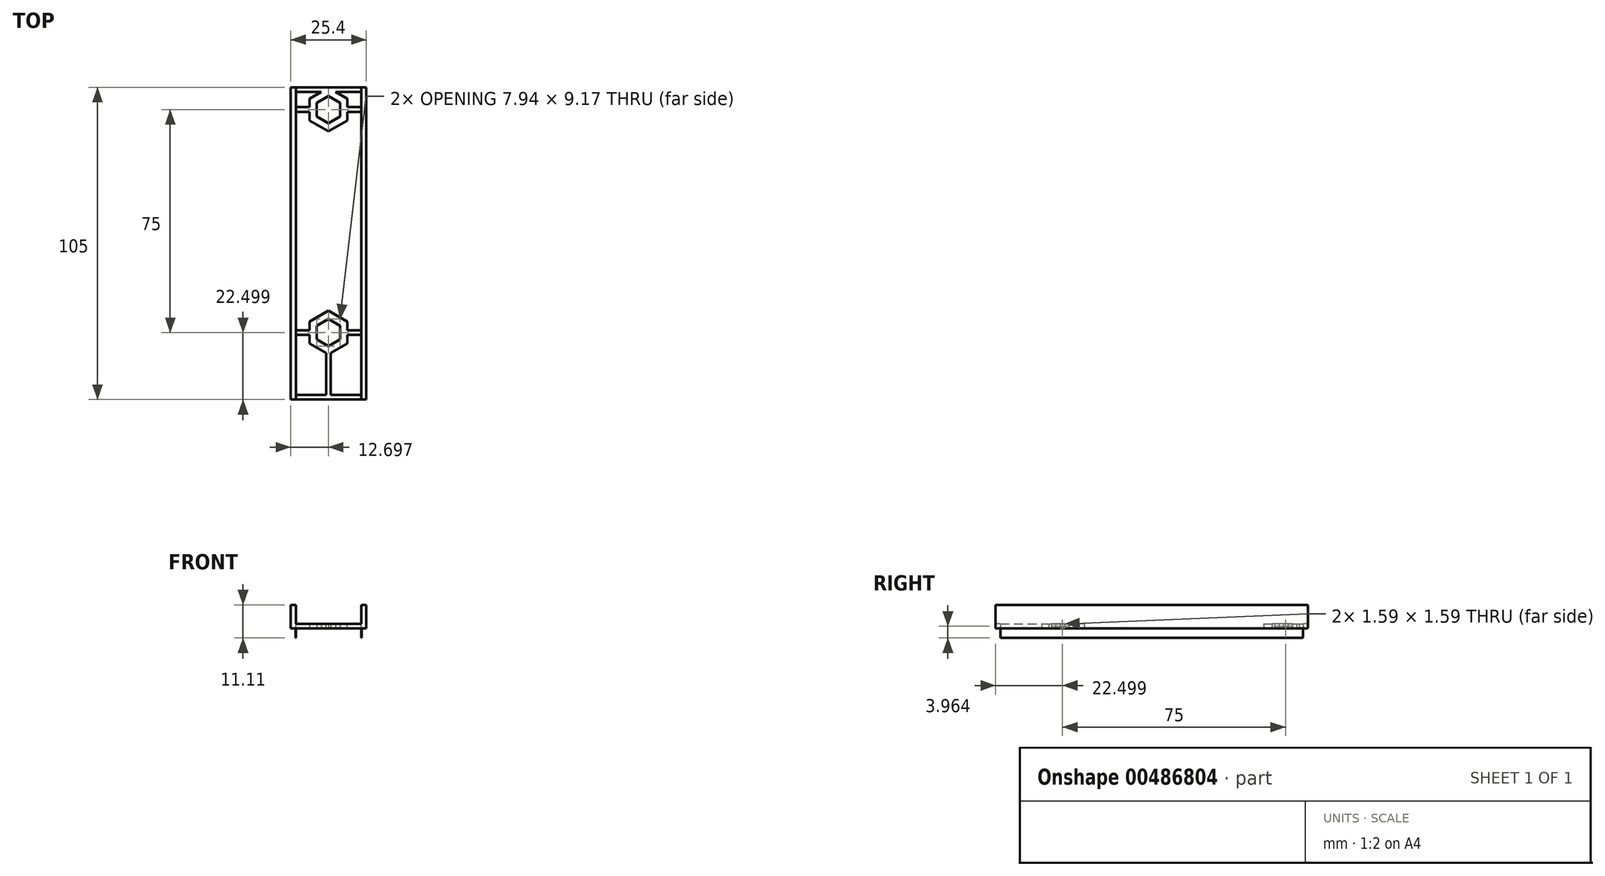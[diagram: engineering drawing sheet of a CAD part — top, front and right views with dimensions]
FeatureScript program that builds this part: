
annotation { "Feature Type Name" : "Feature", "Feature Type Description" : "" }
export const myFeature = defineFeature(function(context is Context, id is Id, definition is map)
    precondition{}
    {
        {
            var Q0;
            Q0=qCreatedBy(makeId("Top.planeOp"),FACE);
            var sketch = newSketch(context, id + "F0", { "sketchPlane" : qUnion([Q0])});
            skLineSegment(sketch, "E0.bottom", {"start": v(-43, -50.26) * mm, "end": v(-68.4, -50.26) * mm});
            skLineSegment(sketch, "E0.top", {"start": v(-43, 54.74) * mm, "end": v(-68.4, 54.74) * mm});
            skLineSegment(sketch, "E0.left", {"start": v(-43, -50.26) * mm, "end": v(-43, 54.74) * mm});
            skLineSegment(sketch, "E0.right", {"start": v(-68.4, -50.26) * mm, "end": v(-68.4, 54.74) * mm});
            skSolve(sketch);
        }
        {
            var Q0;
            Q0 = qSketchRegion(id + "F0", true);
            extrude(context, id + "F1", {"entities" : qUnion([Q0]), "depth" : 12.7 * mm});
        }
        {
            var Q0;
            Q0=makeQuery(id+"F1.opExtrude","CAP_FACE",FACE,{"disambiguationData":[OSD([sQuery(id+"F0.wireOp",EDGE,"E0.bottom"),sQuery(id+"F0.wireOp",EDGE,"E0.top"),sQuery(id+"F0.wireOp",EDGE,"E0.left"),sQuery(id+"F0.wireOp",EDGE,"E0.right")])],"isStart":false});
            var sketch = newSketch(context, id + "F2", { "sketchPlane" : qUnion([Q0])});
            skCircle(sketch, "E1", {"center": v(-55.7, -27.76) * mm, "radius": 1.59 * mm});
            skPoint(sketch, "E1.centerSnap0", {"position": v(-55.7, -50.26) * mm});
            skSolve(sketch);
        }
        {
            var Q0;
            Q0 = qSketchRegion(id + "F2", true);
            extrude(context, id + "F3", {"entities" : qUnion([Q0]), "operationType" : NewBodyOperationType.REMOVE, "oppositeDirection" : true, "depth" : 25.4 * mm});
        }
        {
            var Q0;
            Q0=makeQuery(id+"F1.opExtrude","SWEPT_FACE",FACE,{"disambiguationData":[OSD([sQuery(id+"F0.wireOp",EDGE,"E0.bottom")])]});
            var sketch = newSketch(context, id + "F4", { "sketchPlane" : qUnion([Q0])});
            skCircle(sketch, "E2", {"center": v(-55.7, 19.05) * mm, "radius": 12.7 * mm});
            skSolve(sketch);
        }
        {
            var Q0;
            Q0=makeQuery(id+"F1.opExtrude","CAP_FACE",FACE,{"disambiguationData":[OSD([sQuery(id+"F0.wireOp",EDGE,"E0.bottom"),sQuery(id+"F0.wireOp",EDGE,"E0.top"),sQuery(id+"F0.wireOp",EDGE,"E0.left"),sQuery(id+"F0.wireOp",EDGE,"E0.right")])],"isStart":false});
            var sketch = newSketch(context, id + "F5", { "sketchPlane" : qUnion([Q0])});
            skCircle(sketch, "E3", {"center": v(-55.7, 47.24) * mm, "radius": 1.59 * mm});
            skPoint(sketch, "E3.centerSnap0", {"position": v(-55.7, 54.74) * mm});
            skSolve(sketch);
        }
        {
            var Q0;
            Q0 = qSketchRegion(id + "F5", true);
            extrude(context, id + "F6", {"entities" : qUnion([Q0]), "operationType" : NewBodyOperationType.REMOVE, "oppositeDirection" : true, "depth" : 25.4 * mm});
        }
        {
            var Q0;
            Q0 = qSketchRegion(id + "F4", true);
            extrude(context, id + "F7", {"entities" : qUnion([Q0]), "operationType" : NewBodyOperationType.REMOVE, "endBound" : BoundingType.THROUGH_ALL, "oppositeDirection" : true, "depth" : 25.4 * mm});
        }
        {
            var Q0;
            Q0=makeQuery(id+"F1.opExtrude","SWEPT_FACE",FACE,{"disambiguationData":[OSD([sQuery(id+"F0.wireOp",EDGE,"E0.bottom")])]});
            var sketch = newSketch(context, id + "F8", { "sketchPlane" : qUnion([Q0])});
            skLineSegment(sketch, "E4.bottom", {"start": v(-68.4, 0) * mm, "end": v(-43, 0) * mm});
            skLineSegment(sketch, "E4.top", {"start": v(-68.4, 4.76) * mm, "end": v(-43, 4.76) * mm});
            skLineSegment(sketch, "E4.left", {"start": v(-68.4, 0) * mm, "end": v(-68.4, 4.76) * mm});
            skLineSegment(sketch, "E4.right", {"start": v(-43, 0) * mm, "end": v(-43, 4.76) * mm});
            skSolve(sketch);
        }
        {
            var Q0;
            Q0 = qSketchRegion(id + "F8", true);
            extrude(context, id + "F9", {"entities" : qUnion([Q0]), "operationType" : NewBodyOperationType.REMOVE, "endBound" : BoundingType.THROUGH_ALL, "oppositeDirection" : true, "depth" : 25.4 * mm});
        }
        {
            var Q0;
            Q0=makeQuery(id+"F9.boolean.opBoolean","COPY",FACE,{"derivedFrom":makeQuery(id+"F9.opExtrude","SWEPT_FACE",FACE,{"disambiguationData":[OSD([sQuery(id+"F8.wireOp",EDGE,"E4.top")])]})});
            var sketch = newSketch(context, id + "F10", { "sketchPlane" : qUnion([Q0])});
            skCircle(sketch, "E5.cCircle", {"center": v(-55.7, 27.76) * mm, "radius": 3.97 * mm, "construction": true});
            skLineSegment(sketch, "E5.0", {"start": v(-51.72, 30.05) * mm, "end": v(-51.72, 25.47) * mm});
            skLineSegment(sketch, "E5.1", {"start": v(-51.72, 25.47) * mm, "end": v(-55.7, 23.18) * mm});
            skLineSegment(sketch, "E5.2", {"start": v(-55.7, 23.18) * mm, "end": v(-59.66, 25.47) * mm});
            skLineSegment(sketch, "E5.3", {"start": v(-59.66, 25.47) * mm, "end": v(-59.66, 30.05) * mm});
            skLineSegment(sketch, "E5.4", {"start": v(-59.66, 30.05) * mm, "end": v(-55.7, 32.34) * mm});
            skLineSegment(sketch, "E5.5", {"start": v(-55.7, 32.34) * mm, "end": v(-51.72, 30.05) * mm});
            skPoint(sketch, "E5.0.midPoint", {"position": v(-51.72, 27.76) * mm});
            skCircle(sketch, "E6.cCircle", {"center": v(-55.7, -47.24) * mm, "radius": 3.97 * mm, "construction": true});
            skLineSegment(sketch, "E6.0", {"start": v(-51.72, -44.95) * mm, "end": v(-51.72, -49.53) * mm});
            skLineSegment(sketch, "E6.1", {"start": v(-51.72, -49.53) * mm, "end": v(-55.7, -51.82) * mm});
            skLineSegment(sketch, "E6.2", {"start": v(-55.7, -51.82) * mm, "end": v(-59.66, -49.53) * mm});
            skLineSegment(sketch, "E6.3", {"start": v(-59.66, -49.53) * mm, "end": v(-59.66, -44.95) * mm});
            skLineSegment(sketch, "E6.4", {"start": v(-59.66, -44.95) * mm, "end": v(-55.7, -42.66) * mm});
            skLineSegment(sketch, "E6.5", {"start": v(-55.7, -42.66) * mm, "end": v(-51.72, -44.95) * mm});
            skPoint(sketch, "E6.0.midPoint", {"position": v(-51.72, -47.24) * mm});
            skSolve(sketch);
        }
        {
            var Q0;
            Q0 = qSketchRegion(id + "F10", true);
            extrude(context, id + "F11", {"entities" : qUnion([Q0]), "operationType" : NewBodyOperationType.REMOVE, "oppositeDirection" : true, "depth" : 25.4 * mm});
        }
        {
            var Q0;
            Q0=makeQuery(id+"F9.boolean.opBoolean","COPY",FACE,{"derivedFrom":makeQuery(id+"F9.opExtrude","SWEPT_FACE",FACE,{"disambiguationData":[OSD([sQuery(id+"F8.wireOp",EDGE,"E4.top")])]})});
            extrude(context, id + "F12", {"entities" : qUnion([Q0]), "operationType" : NewBodyOperationType.ADD, "depth" : 1 / 203.2 * mm});
        }
        {
            var Q0;
            Q0=makeQuery(id+"F12.opExtrude","CAP_FACE",FACE,{"disambiguationData":[OSD([sQuery(id+"F8.wireOp",EDGE,"E4.top")])],"isStart":false});
            var sketch = newSketch(context, id + "F13", { "sketchPlane" : qUnion([Q0])});
            skCircle(sketch, "E7.cCircle", {"center": v(-55.7, -47.24) * mm, "radius": 6.35 * mm, "construction": true});
            skPoint(sketch, "E7.cCircle.centerSnap0", {"position": v(-51.72, -47.24) * mm});
            skLineSegment(sketch, "E7.0", {"start": v(-62.04, -43.57) * mm, "end": v(-55.7, -39.9) * mm});
            skLineSegment(sketch, "E7.1", {"start": v(-55.7, -39.9) * mm, "end": v(-49.34, -43.57) * mm});
            skLineSegment(sketch, "E7.2", {"start": v(-49.34, -43.57) * mm, "end": v(-49.34, -50.9) * mm});
            skLineSegment(sketch, "E7.3", {"start": v(-49.34, -50.9) * mm, "end": v(-55.7, -54.57) * mm});
            skLineSegment(sketch, "E7.4", {"start": v(-55.7, -54.57) * mm, "end": v(-62.04, -50.9) * mm});
            skLineSegment(sketch, "E7.5", {"start": v(-62.04, -50.9) * mm, "end": v(-62.04, -43.57) * mm});
            skPoint(sketch, "E7.0.midPoint", {"position": v(-58.87, -41.74) * mm});
            skCircle(sketch, "E8.cCircle", {"center": v(-55.7, 27.76) * mm, "radius": 6.35 * mm, "construction": true});
            skPoint(sketch, "E8.cCircle.centerSnap0", {"position": v(-51.72, 27.76) * mm});
            skLineSegment(sketch, "E8.0", {"start": v(-62.04, 24.1) * mm, "end": v(-62.04, 31.43) * mm});
            skLineSegment(sketch, "E8.1", {"start": v(-62.04, 31.43) * mm, "end": v(-55.7, 35.1) * mm});
            skLineSegment(sketch, "E8.2", {"start": v(-55.7, 35.1) * mm, "end": v(-49.34, 31.43) * mm});
            skLineSegment(sketch, "E8.3", {"start": v(-49.34, 31.43) * mm, "end": v(-49.34, 24.1) * mm});
            skLineSegment(sketch, "E8.4", {"start": v(-49.34, 24.1) * mm, "end": v(-55.7, 20.43) * mm});
            skLineSegment(sketch, "E8.5", {"start": v(-55.7, 20.43) * mm, "end": v(-62.04, 24.1) * mm});
            skPoint(sketch, "E8.0.midPoint", {"position": v(-62.04, 27.76) * mm});
            skLineSegment(sketch, "E9", {"start": v(-53.23, -53.15) * mm, "end": v(-44.58, -53.15) * mm});
            skLineSegment(sketch, "E10", {"start": v(-44.58, -53.15) * mm, "end": v(-44.58, 48.67) * mm});
            skLineSegment(sketch, "E11", {"start": v(-44.58, 48.67) * mm, "end": v(-66.8, 48.67) * mm});
            skLineSegment(sketch, "E12", {"start": v(-66.8, 48.67) * mm, "end": v(-66.8, -53.15) * mm});
            skLineSegment(sketch, "E13", {"start": v(-66.8, -53.15) * mm, "end": v(-58.15, -53.15) * mm});
            skSolve(sketch);
        }
        {
            var Q0;
            Q0=makeQuery(id+"F13.imprint","IMPRINT",FACE,{"disambiguationData":[TD([[makeQuery(id+"F13.imprint","IMPRINT",EDGE,{"derivedFrom":sQuery(id+"F13.wireOp",EDGE,"E7.0")}),1.0]])]});
            extrude(context, id + "F14", {"entities" : qUnion([Q0]), "operationType" : NewBodyOperationType.REMOVE, "endBound" : BoundingType.THROUGH_ALL, "oppositeDirection" : true, "depth" : 25.4 * mm});
        }
        {
            var Q0;
            {var subQ3=sQuery(id+"F8.wireOp",EDGE,"E4.top");var subQ9=sQuery(id+"F0.wireOp",EDGE,"E0.bottom");Q0=makeQuery(id+"F14.boolean.opBoolean","SPLIT",FACE,{"disambiguationData":[TD([makeQuery(id+"F1.opExtrude","SWEPT_FACE",FACE,{"disambiguationData":[OSD([subQ9])]})])],"derivedFrom":makeQuery(id+"F12.opExtrude","CAP_FACE",FACE,{"disambiguationData":[OSD([subQ3])],"isStart":false})});}
            var sketch = newSketch(context, id + "F15", { "sketchPlane" : qUnion([Q0])});
            skLineSegment(sketch, "E14.bottom", {"start": v(-49.34, -48.03) * mm, "end": v(-43, -48.03) * mm});
            skLineSegment(sketch, "E14.top", {"start": v(-49.34, -46.44) * mm, "end": v(-43, -46.44) * mm});
            skLineSegment(sketch, "E14.left", {"start": v(-49.34, -48.03) * mm, "end": v(-49.34, -46.44) * mm});
            skLineSegment(sketch, "E14.right", {"start": v(-43, -48.03) * mm, "end": v(-43, -46.44) * mm});
            skLineSegment(sketch, "E15.bottom", {"start": v(-62.04, -48.03) * mm, "end": v(-68.4, -48.03) * mm});
            skLineSegment(sketch, "E15.top", {"start": v(-62.04, -46.44) * mm, "end": v(-68.4, -46.44) * mm});
            skLineSegment(sketch, "E15.left", {"start": v(-62.04, -48.03) * mm, "end": v(-62.04, -46.44) * mm});
            skLineSegment(sketch, "E15.right", {"start": v(-68.4, -48.03) * mm, "end": v(-68.4, -46.44) * mm});
            skSolve(sketch);
        }
        {
            var Q0;
            {var subQ0=sQuery(id+"F15.wireOp",EDGE,"E14.left");Q0=makeQuery(id+"F15.imprint","IMPRINT",FACE,{"disambiguationData":[TD([[makeQuery(id+"F15.imprint","IMPRINT",EDGE,{"derivedFrom":subQ0}),1.0]])]});}
            var Q1;
            {var subQ0=sQuery(id+"F15.wireOp",EDGE,"E15.left");Q1=makeQuery(id+"F15.imprint","IMPRINT",FACE,{"disambiguationData":[TD([[makeQuery(id+"F15.imprint","IMPRINT",EDGE,{"derivedFrom":subQ0}),1.0]])]});}
            extrude(context, id + "F16", {"entities" : qUnion([Q0, Q1]), "operationType" : NewBodyOperationType.ADD, "oppositeDirection" : true, "depth" : 6.35 * mm});
        }
        {
            var Q0;
            {var subQ0=sQuery(id+"F13.wireOp",EDGE,"E12");var subQ1=sQuery(id+"F13.wireOp",EDGE,"E10");var subQ5=sQuery(id+"F8.wireOp",EDGE,"E4.top");var subQ11=sQuery(id+"F0.wireOp",EDGE,"E0.bottom");Q0=makeQuery(id+"F16.boolean.opBoolean","MERGE",FACE,{"derivedFrom":[makeQuery(id+"F14.boolean.opBoolean","SPLIT",FACE,{"disambiguationData":[TD([makeQuery(id+"F1.opExtrude","SWEPT_FACE",FACE,{"disambiguationData":[OSD([subQ11])]})])],"derivedFrom":makeQuery(id+"F12.opExtrude","CAP_FACE",FACE,{"disambiguationData":[OSD([subQ5])],"isStart":false})}),makeQuery(id+"F16.opExtrude","CAP_FACE",FACE,{"disambiguationData":[OSD([subQ1,sQuery(id+"F15.wireOp",EDGE,"E14.bottom"),sQuery(id+"F15.wireOp",EDGE,"E14.top"),sQuery(id+"F15.wireOp",EDGE,"E14.left")])],"isStart":true}),makeQuery(id+"F16.opExtrude","CAP_FACE",FACE,{"disambiguationData":[OSD([subQ0,sQuery(id+"F15.wireOp",EDGE,"E15.bottom"),sQuery(id+"F15.wireOp",EDGE,"E15.top"),sQuery(id+"F15.wireOp",EDGE,"E15.left")])],"isStart":true})]});}
            var sketch = newSketch(context, id + "F17", { "sketchPlane" : qUnion([Q0])});
            skLineSegment(sketch, "E16.bottom", {"start": v(-61.05, 28.56) * mm, "end": v(-66.8, 28.56) * mm});
            skLineSegment(sketch, "E16.top", {"start": v(-61.05, 26.97) * mm, "end": v(-66.8, 26.97) * mm});
            skLineSegment(sketch, "E16.left", {"start": v(-61.05, 28.56) * mm, "end": v(-61.05, 26.97) * mm});
            skLineSegment(sketch, "E16.right", {"start": v(-66.8, 28.56) * mm, "end": v(-66.8, 26.97) * mm});
            skPoint(sketch, "E17.firstSnap0", {"position": v(-63.93, 26.97) * mm});
            skLineSegment(sketch, "E17.bottom", {"start": v(-50.1, 26.97) * mm, "end": v(-44.58, 26.97) * mm});
            skLineSegment(sketch, "E17.top", {"start": v(-50.1, 28.56) * mm, "end": v(-44.58, 28.56) * mm});
            skLineSegment(sketch, "E17.left", {"start": v(-50.1, 26.97) * mm, "end": v(-50.1, 28.56) * mm});
            skLineSegment(sketch, "E17.right", {"start": v(-44.58, 26.97) * mm, "end": v(-44.58, 28.56) * mm});
            skLineSegment(sketch, "E18.bottom", {"start": v(-56.49, 33.74) * mm, "end": v(-54.9, 33.74) * mm});
            skLineSegment(sketch, "E18.top", {"start": v(-56.49, 48.67) * mm, "end": v(-54.9, 48.67) * mm});
            skLineSegment(sketch, "E18.left", {"start": v(-56.49, 33.74) * mm, "end": v(-56.49, 48.67) * mm});
            skLineSegment(sketch, "E18.right", {"start": v(-54.9, 33.74) * mm, "end": v(-54.9, 48.67) * mm});
            skSolve(sketch);
        }
        {
            var Q0;
            Q0 = qSketchRegion(id + "F17", true);
            extrude(context, id + "F18", {"entities" : qUnion([Q0]), "oppositeDirection" : true, "depth" : 4.23 * mm});
        }
        {
            var Q0;
            Q0=makeQuery(id+"F18.opExtrude","SWEPT_BODY",BODY,{"disambiguationData":[OSD([sQuery(id+"F17.wireOp",EDGE,"E17.bottom"),sQuery(id+"F17.wireOp",EDGE,"E17.top"),sQuery(id+"F17.wireOp",EDGE,"E17.left"),sQuery(id+"F17.wireOp",EDGE,"E17.right")])]});
            var Q1;
            Q1=makeQuery(id+"F18.opExtrude","SWEPT_BODY",BODY,{"disambiguationData":[OSD([sQuery(id+"F17.wireOp",EDGE,"E18.bottom"),sQuery(id+"F17.wireOp",EDGE,"E18.top"),sQuery(id+"F17.wireOp",EDGE,"E18.left"),sQuery(id+"F17.wireOp",EDGE,"E18.right")])]});
            var Q2;
            Q2=makeQuery(id+"F14.boolean.opBoolean","SPLIT",BODY,{"disambiguationData":[OD(0.0)],"derivedFrom":makeQuery(id+"F1.opExtrude","SWEPT_BODY",BODY,{"disambiguationData":[OSD([sQuery(id+"F0.wireOp",EDGE,"E0.bottom"),sQuery(id+"F0.wireOp",EDGE,"E0.top"),sQuery(id+"F0.wireOp",EDGE,"E0.left"),sQuery(id+"F0.wireOp",EDGE,"E0.right")])]})});
            var Q3;
            Q3=makeQuery(id+"F14.boolean.opBoolean","SPLIT",BODY,{"disambiguationData":[OD(1.0)],"derivedFrom":makeQuery(id+"F1.opExtrude","SWEPT_BODY",BODY,{"disambiguationData":[OSD([sQuery(id+"F0.wireOp",EDGE,"E0.bottom"),sQuery(id+"F0.wireOp",EDGE,"E0.top"),sQuery(id+"F0.wireOp",EDGE,"E0.left"),sQuery(id+"F0.wireOp",EDGE,"E0.right")])]})});
            var Q4;
            Q4=makeQuery(id+"F18.opExtrude","SWEPT_BODY",BODY,{"disambiguationData":[OSD([sQuery(id+"F17.wireOp",EDGE,"E16.bottom"),sQuery(id+"F17.wireOp",EDGE,"E16.top"),sQuery(id+"F17.wireOp",EDGE,"E16.left"),sQuery(id+"F17.wireOp",EDGE,"E16.right")])]});
            booleanBodies(context, id + "F19", {"operationType" : BooleanOperationType.UNION, "tools" : qUnion([Q0, Q1, Q2, Q3, Q4])});
        }
        {
            var Q0;
            {var subQ0=sQuery(id+"F0.wireOp",EDGE,"E0.bottom");var subQ1=sQuery(id+"F0.wireOp",EDGE,"E0.top");var subQ2=sQuery(id+"F0.wireOp",EDGE,"E0.left");Q0=makeQuery(id+"F7.boolean.opBoolean","SPLIT",FACE,{"disambiguationData":[TD([makeQuery(id+"F1.opExtrude","SWEPT_FACE",FACE,{"disambiguationData":[OSD([subQ2])]})])],"derivedFrom":makeQuery(id+"F1.opExtrude","CAP_FACE",FACE,{"disambiguationData":[OSD([subQ0,subQ1,subQ2,sQuery(id+"F0.wireOp",EDGE,"E0.right")])],"isStart":false})});}
            var sketch = newSketch(context, id + "F20", { "sketchPlane" : qUnion([Q0])});
            skLineSegment(sketch, "E19.bottom", {"start": v(-44.7, -50.26) * mm, "end": v(-44.58, -50.26) * mm});
            skLineSegment(sketch, "E19.top", {"start": v(-44.7, 53.15) * mm, "end": v(-44.58, 53.15) * mm});
            skLineSegment(sketch, "E19.left", {"start": v(-44.7, -50.26) * mm, "end": v(-44.7, 53.15) * mm});
            skLineSegment(sketch, "E19.right", {"start": v(-44.58, -50.26) * mm, "end": v(-44.58, 53.15) * mm});
            skSolve(sketch);
        }
        {
            var Q0;
            {var subQ0=sQuery(id+"F0.wireOp",EDGE,"E0.bottom");var subQ1=sQuery(id+"F0.wireOp",EDGE,"E0.right");var subQ2=sQuery(id+"F0.wireOp",EDGE,"E0.top");Q0=makeQuery(id+"F7.boolean.opBoolean","SPLIT",FACE,{"disambiguationData":[TD([makeQuery(id+"F1.opExtrude","SWEPT_FACE",FACE,{"disambiguationData":[OSD([subQ1])]})])],"derivedFrom":makeQuery(id+"F1.opExtrude","CAP_FACE",FACE,{"disambiguationData":[OSD([subQ0,subQ2,sQuery(id+"F0.wireOp",EDGE,"E0.left"),subQ1])],"isStart":false})});}
            var sketch = newSketch(context, id + "F21", { "sketchPlane" : qUnion([Q0])});
            skLineSegment(sketch, "E20.bottom", {"start": v(-66.7, 53.15) * mm, "end": v(-66.8, 53.15) * mm});
            skLineSegment(sketch, "E20.top", {"start": v(-66.7, -48.67) * mm, "end": v(-66.8, -48.67) * mm});
            skLineSegment(sketch, "E20.left", {"start": v(-66.7, 53.15) * mm, "end": v(-66.7, -48.67) * mm});
            skLineSegment(sketch, "E20.right", {"start": v(-66.8, 53.15) * mm, "end": v(-66.8, -48.67) * mm});
            skSolve(sketch);
        }
        {
            var Q0;
            {var subQ0=sQuery(id+"F20.wireOp",EDGE,"E19.top");Q0=makeQuery(id+"F20.imprint","IMPRINT",FACE,{"disambiguationData":[TD([[makeQuery(id+"F20.imprint","IMPRINT",EDGE,{"derivedFrom":subQ0}),1.0]])]});}
            var Q1;
            Q1=makeQuery(id+"F21.imprint","IMPRINT",FACE,{"disambiguationData":[TD([[makeQuery(id+"F21.imprint","IMPRINT",EDGE,{"derivedFrom":sQuery(id+"F21.wireOp",EDGE,"E20.bottom")}),1.0]])]});
            extrude(context, id + "F22", {"entities" : qUnion([Q0, Q1]), "operationType" : NewBodyOperationType.ADD, "oppositeDirection" : true, "depth" : 12.7 * mm});
        }
        {
            var Q0;
            {var subQ0=sQuery(id+"F0.wireOp",EDGE,"E0.top");Q0=makeQuery(id+"F12.boolean.opBoolean","MERGE",FACE,{"derivedFrom":[makeQuery(id+"F1.opExtrude","SWEPT_FACE",FACE,{"disambiguationData":[OSD([subQ0])]}),makeQuery(id+"F12.opExtrude","SWEPT_FACE",FACE,{"disambiguationData":[OSD([subQ0,sQuery(id+"F8.wireOp",EDGE,"E4.top")])]})]});}
            var sketch = newSketch(context, id + "F23", { "sketchPlane" : qUnion([Q0])});
            skLineSegment(sketch, "E21.bottom", {"start": v(68.4, 1.59) * mm, "end": v(43, 1.59) * mm});
            skLineSegment(sketch, "E21.top", {"start": v(68.4, -4.13) * mm, "end": v(43, -4.13) * mm});
            skLineSegment(sketch, "E21.left", {"start": v(68.4, 1.59) * mm, "end": v(68.4, -4.13) * mm});
            skLineSegment(sketch, "E21.right", {"start": v(43, 1.59) * mm, "end": v(43, -4.13) * mm});
            skSolve(sketch);
        }
        {
            var Q0;
            Q0 = qSketchRegion(id + "F23", true);
            extrude(context, id + "F24", {"entities" : qUnion([Q0]), "operationType" : NewBodyOperationType.REMOVE, "endBound" : BoundingType.THROUGH_ALL, "oppositeDirection" : true, "depth" : 25.4 * mm});
        }
        {
            var Q0;
            Q0=makeQuery(id+"F12.boolean.opBoolean","MERGE",FACE,{"derivedFrom":[makeQuery(id+"F1.opExtrude","SWEPT_FACE",FACE,{"disambiguationData":[OSD([sQuery(id+"F0.wireOp",EDGE,"E0.bottom")])]}),makeQuery(id+"F12.opExtrude","SWEPT_FACE",FACE,{"disambiguationData":[OSD([sQuery(id+"F8.wireOp",EDGE,"E4.top")])]})]});
            var sketch = newSketch(context, id + "F25", { "sketchPlane" : qUnion([Q0])});
            skPoint(sketch, "E22.oppositeSnap0", {"position": v(-55.7, 6.35) * mm});
            skLineSegment(sketch, "E22.bottom", {"start": v(-66.7, 12.7) * mm, "end": v(-44.7, 12.7) * mm});
            skLineSegment(sketch, "E22.top", {"start": v(-66.7, 6.35) * mm, "end": v(-44.7, 6.35) * mm});
            skLineSegment(sketch, "E22.left", {"start": v(-66.7, 12.7) * mm, "end": v(-66.7, 6.35) * mm});
            skLineSegment(sketch, "E22.right", {"start": v(-44.7, 12.7) * mm, "end": v(-44.7, 6.35) * mm});
            skSolve(sketch);
        }
        {
            var Q0;
            Q0 = qSketchRegion(id + "F25", true);
            extrude(context, id + "F26", {"entities" : qUnion([Q0]), "operationType" : NewBodyOperationType.REMOVE, "endBound" : BoundingType.THROUGH_ALL, "oppositeDirection" : true, "depth" : 25.4 * mm});
        }
        {
            var Q0;
            Q0=makeQuery(id+"F14.boolean.opBoolean","COPY",FACE,{"derivedFrom":makeQuery(id+"F14.opExtrude","SWEPT_FACE",FACE,{"disambiguationData":[OSD([sQuery(id+"F13.wireOp",EDGE,"E8.0")])]})});
            var sketch = newSketch(context, id + "F27", { "sketchPlane" : qUnion([Q0])});
            skLineSegment(sketch, "E23.bottom", {"start": v(26.97, 5.82) * mm, "end": v(28.56, 5.82) * mm});
            skLineSegment(sketch, "E23.top", {"start": v(26.97, 6.35) * mm, "end": v(28.56, 6.35) * mm});
            skLineSegment(sketch, "E23.left", {"start": v(26.97, 5.82) * mm, "end": v(26.97, 6.35) * mm});
            skLineSegment(sketch, "E23.right", {"start": v(28.56, 5.82) * mm, "end": v(28.56, 6.35) * mm});
            skSolve(sketch);
        }
        {
            var Q0;
            Q0 = qSketchRegion(id + "F27", true);
            extrude(context, id + "F28", {"entities" : qUnion([Q0]), "operationType" : NewBodyOperationType.ADD, "depth" : 6.35 * mm});
        }
        {
            var Q0;
            Q0=makeQuery(id+"F14.boolean.opBoolean","COPY",FACE,{"derivedFrom":makeQuery(id+"F14.opExtrude","SWEPT_FACE",FACE,{"disambiguationData":[OSD([sQuery(id+"F13.wireOp",EDGE,"E8.3")])]})});
            var sketch = newSketch(context, id + "F29", { "sketchPlane" : qUnion([Q0])});
            skLineSegment(sketch, "E24.bottom", {"start": v(-28.56, 5.82) * mm, "end": v(-26.97, 5.82) * mm});
            skLineSegment(sketch, "E24.top", {"start": v(-28.56, 6.35) * mm, "end": v(-26.97, 6.35) * mm});
            skLineSegment(sketch, "E24.left", {"start": v(-28.56, 5.82) * mm, "end": v(-28.56, 6.35) * mm});
            skLineSegment(sketch, "E24.right", {"start": v(-26.97, 5.82) * mm, "end": v(-26.97, 6.35) * mm});
            skSolve(sketch);
        }
        {
            var Q0;
            Q0 = qSketchRegion(id + "F29", true);
            extrude(context, id + "F30", {"entities" : qUnion([Q0]), "operationType" : NewBodyOperationType.ADD, "depth" : 6.35 * mm});
        }
        {
            var Q0;
            Q0=makeQuery(id+"F14.boolean.opBoolean","COPY",FACE,{"derivedFrom":makeQuery(id+"F14.opExtrude","SWEPT_FACE",FACE,{"disambiguationData":[OSD([sQuery(id+"F13.wireOp",EDGE,"E11")])]})});
            var sketch = newSketch(context, id + "F31", { "sketchPlane" : qUnion([Q0])});
            skLineSegment(sketch, "E25.bottom", {"start": v(54.9, 5.82) * mm, "end": v(56.49, 5.82) * mm});
            skLineSegment(sketch, "E25.top", {"start": v(54.9, 6.35) * mm, "end": v(56.49, 6.35) * mm});
            skLineSegment(sketch, "E25.left", {"start": v(54.9, 5.82) * mm, "end": v(54.9, 6.35) * mm});
            skLineSegment(sketch, "E25.right", {"start": v(56.49, 5.82) * mm, "end": v(56.49, 6.35) * mm});
            skSolve(sketch);
        }
        {
            var Q0;
            Q0 = qSketchRegion(id + "F31", true);
            extrude(context, id + "F32", {"entities" : qUnion([Q0]), "operationType" : NewBodyOperationType.ADD, "depth" : 15.24 * mm});
        }
    });
